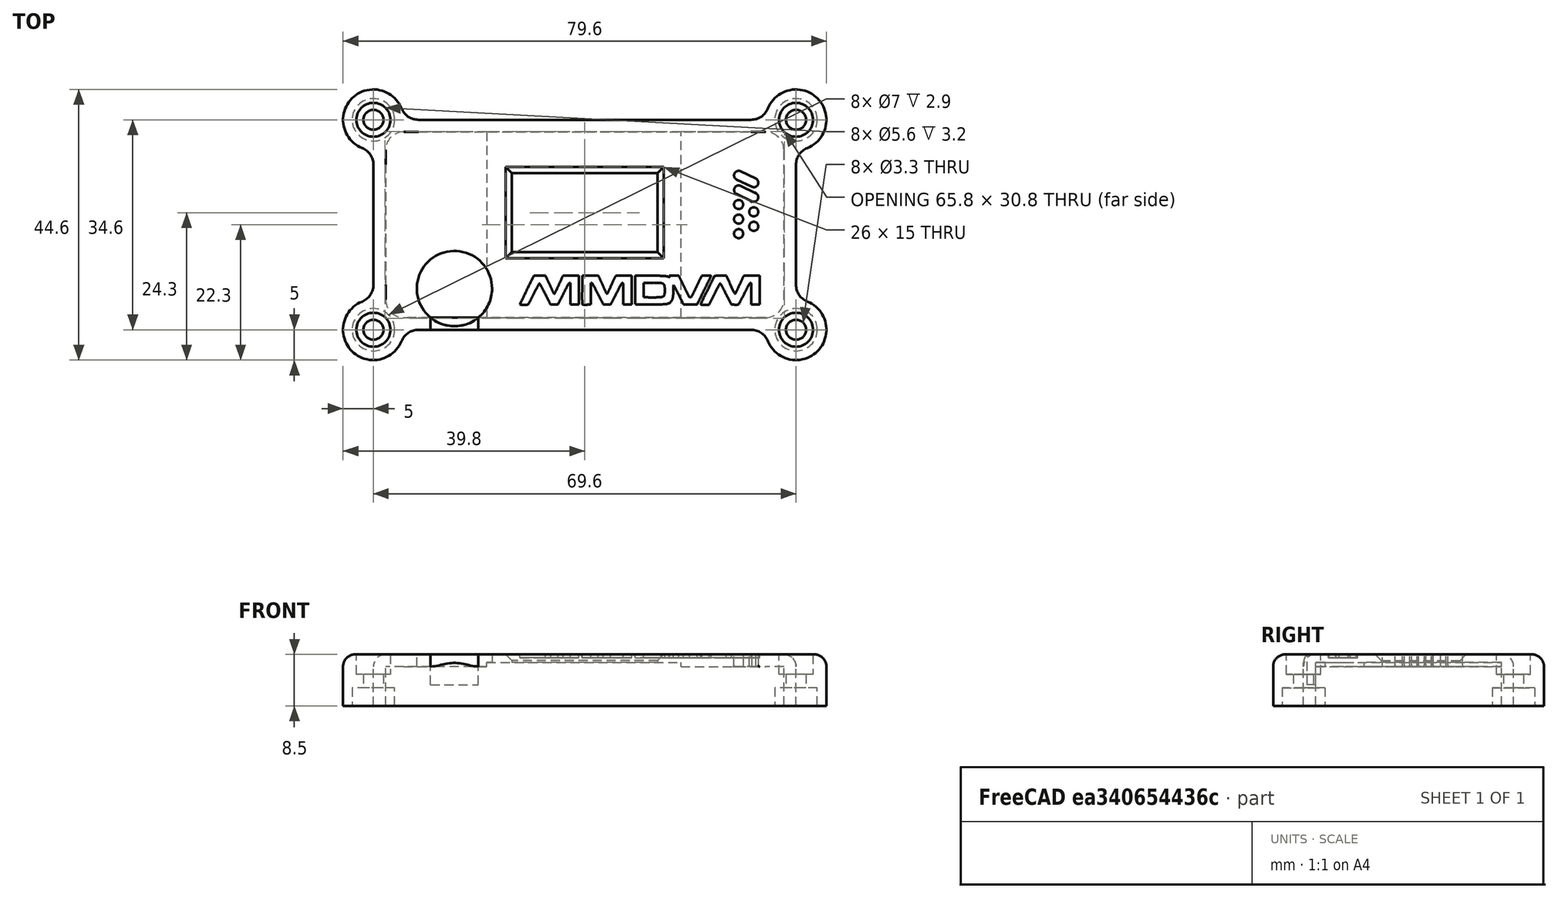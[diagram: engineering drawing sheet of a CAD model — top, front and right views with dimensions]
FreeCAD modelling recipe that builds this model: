
FCSTD DOCUMENT  (FreeCAD 0.18R13934 (Git))
Label: MMDVM_HS_Top-PCB-v1.6-SLIM
License: CreativeCommons Attribution-NonCommercial-ShareAlike
LicenseURL: http://creativecommons.org/licenses/by-nc-sa/4.0/
objects: Sketcher::SketchObject×11, PartDesign::Pocket×6, Part::Feature×5, PartDesign::Fillet×4, Part::Cut×2, Part::FeaturePython×2, PartDesign::Pad×1, PartDesign::Chamfer×1, PartDesign::Hole×1, Part::MultiFuse×1, PartDesign::Body×1, Part::Extrusion×1, Mesh::Feature×1
note: 44 computed .brp shape members not serialized (recipe doc carries the construction recipe); baked Part::Feature solids carry a one-line shape summary decoded from their .brp

FEATURE [Sketcher::SketchObject] Sketch
  MapMode = 5
  Support = -> [XY_Plane]
  sketch-geometry (24):
    g0: LineSegment [constr] StartX=-32.5 StartY=15 StartZ=0 EndX=32.5 EndY=15 EndZ=0
    g1: LineSegment [constr] StartX=32.5 StartY=15 StartZ=0 EndX=32.5 EndY=-15 EndZ=0
    g2: LineSegment [constr] StartX=32.5 StartY=-15 StartZ=0 EndX=-32.5 EndY=-15 EndZ=0
    g3: LineSegment [constr] StartX=-32.5 StartY=-15 StartZ=0 EndX=-32.5 EndY=15 EndZ=0
    g4: LineSegment [constr] StartX=-29 StartY=11.5 StartZ=0 EndX=29 EndY=11.5 EndZ=0
    g5: LineSegment [constr] StartX=29 StartY=11.5 StartZ=0 EndX=29 EndY=-11.5 EndZ=0
    g6: LineSegment [constr] StartX=29 StartY=-11.5 StartZ=0 EndX=-29 EndY=-11.5 EndZ=0
    g7: LineSegment [constr] StartX=-29 StartY=-11.5 StartZ=0 EndX=-29 EndY=11.5 EndZ=0
    g8: Circle CenterX=-29 CenterY=11.5 CenterZ=0 NormalX=0 NormalY=0 NormalZ=1 AngleXU=0 Radius=1.375
    g9: Circle CenterX=29 CenterY=11.5 CenterZ=0 NormalX=0 NormalY=0 NormalZ=1 AngleXU=0 Radius=1.375
    g10: Circle CenterX=29 CenterY=-11.5 CenterZ=0 NormalX=0 NormalY=0 NormalZ=1 AngleXU=0 Radius=1.375
    g11: Circle CenterX=-29 CenterY=-11.5 CenterZ=0 NormalX=0 NormalY=0 NormalZ=1 AngleXU=0 Radius=1.375
    g12: LineSegment [constr] StartX=-29.5 StartY=12 StartZ=0 EndX=29.5 EndY=12 EndZ=0
    g13: LineSegment [constr] StartX=29.5 StartY=12 StartZ=0 EndX=29.5 EndY=-12 EndZ=0
    g14: LineSegment [constr] StartX=29.5 StartY=-12 StartZ=0 EndX=-29.5 EndY=-12 EndZ=0
    g15: LineSegment [constr] StartX=-29.5 StartY=-12 StartZ=0 EndX=-29.5 EndY=12 EndZ=0
    g16: ArcOfCircle CenterX=-29.5 CenterY=12 CenterZ=0 NormalX=0 NormalY=0 NormalZ=1 AngleXU=0 Radius=3 StartAngle=1.5708 EndAngle=3.1416
    g17: ArcOfCircle CenterX=29.5 CenterY=12 CenterZ=0 NormalX=0 NormalY=0 NormalZ=1 AngleXU=0 Radius=3 StartAngle=1.42077e-07 EndAngle=1.5708
    g18: ArcOfCircle CenterX=29.5 CenterY=-12 CenterZ=0 NormalX=0 NormalY=0 NormalZ=1 AngleXU=0 Radius=3 StartAngle=4.71239 EndAngle=6.28319
    g19: ArcOfCircle CenterX=-29.5 CenterY=-12 CenterZ=0 NormalX=0 NormalY=0 NormalZ=1 AngleXU=0 Radius=3 StartAngle=3.14159 EndAngle=4.71239
    g20: LineSegment StartX=-29.5 StartY=15 StartZ=0 EndX=29.5 EndY=15 EndZ=0
    g21: LineSegment StartX=32.5 StartY=12 StartZ=0 EndX=32.5 EndY=-12 EndZ=0
    g22: LineSegment StartX=29.5 StartY=-15 StartZ=0 EndX=-29.5 EndY=-15 EndZ=0
    g23: LineSegment StartX=-32.5 StartY=-12 StartZ=0 EndX=-32.5 EndY=12 EndZ=0
  constraints (68):
    c: Coincident(g0,g1)
    c: Coincident(g1,g2)
    c: Coincident(g2,g3)
    c: Coincident(g3,g0)
    c: Horizontal(g0)
    c: Horizontal(g2)
    c: Vertical(g1)
    c: Vertical(g3)
    c: DistanceX(g0,g0) = 65
    c: DistanceY(g1,g1) = 30
    c: Symmetric(g0,g0,g-2)
    c: Symmetric(g0,g1,g-1)
    c: Coincident(g4,g5)
    c: Coincident(g5,g6)
    c: Coincident(g6,g7)
    c: Coincident(g7,g4)
    c: Horizontal(g4)
    c: Horizontal(g6)
    c: Vertical(g5)
    c: Vertical(g7)
    c: DistanceX(g4,g4) = 58
    c: DistanceY(g5,g5) = 23
    c: Symmetric(g4,g5,g-1)
    c: Symmetric(g4,g4,g-2)
    c: Coincident(g8,g4)
    c: Coincident(g9,g4)
    c: Coincident(g10,g5)
    c: Coincident(g11,g6)
    c: Radius(g11) = 1.375
    c: Radius(g8) = 1.375
    c: Radius(g9) = 1.375
    c: Radius(g10) = 1.375
    c: Coincident(g12,g13)
    c: Coincident(g13,g14)
    c: Coincident(g14,g15)
    c: Coincident(g15,g12)
    c: Horizontal(g12)
    c: Horizontal(g14)
    c: Vertical(g13)
    c: Vertical(g15)
    c: DistanceX(g4,g12) = 0.5
    c: DistanceY(g4,g12) = 0.5
    c: DistanceY(g13,g5) = 0.5
    c: DistanceX(g14,g6) = 0.5
    c: Coincident(g16,g12)
    c: Radius(g16) = 3
    c: Coincident(g17,g12)
    c: Radius(g17) = 3
    c: Coincident(g18,g13)
    c: Radius(g18) = 3
    c: Coincident(g19,g14)
    c: Radius(g19) = 3
    c: PointOnObject(g16,g0)
    c: PointOnObject(g17,g1)
    c: PointOnObject(g18,g2)
    c: PointOnObject(g19,g3)
    c: Coincident(g20,g16)
    c: Horizontal(g20)
    c: Coincident(g20,g17)
    c: Coincident(g21,g17)
    c: Vertical(g21)
    c: Coincident(g18,g21)
    c: Coincident(g22,g18)
    c: Horizontal(g22)
    c: Coincident(g19,g22)
    c: Coincident(g23,g19)
    c: Vertical(g23)
    c: Coincident(g23,g16)
FEATURE [Sketcher::SketchObject] Sketch001
  MapMode = 5
  Support = -> [XY_Plane]
  expr: Constraints[8] = Sketch.Constraints[8]
  expr: Constraints[41] = Sketch.Constraints[41]
  expr: Constraints[9] = Sketch.Constraints[9]
  expr: Constraints[45] = Sketch.Constraints[45]
  expr: Constraints[43] = Sketch.Constraints[43]
  expr: Constraints[42] = Sketch.Constraints[42]
  expr: Constraints[20] = Sketch.Constraints[20]
  expr: Constraints[21] = Sketch.Constraints[21]
  expr: Constraints[28] = Sketch.Constraints[28]
  expr: Constraints[29] = Sketch.Constraints[29]
  expr: Constraints[30] = Sketch.Constraints[30]
  expr: Constraints[40] = Sketch.Constraints[40]
  expr: Constraints[31] = Sketch.Constraints[31]
  expr: Constraints[47] = Sketch.Constraints[47]
  expr: Constraints[49] = Sketch.Constraints[49]
  expr: Constraints[51] = Sketch.Constraints[51]
  sketch-geometry (64):
    g0: LineSegment [constr] StartX=-32.5 StartY=15 StartZ=0 EndX=32.5 EndY=15 EndZ=0
    g1: LineSegment [constr] StartX=32.5 StartY=15 StartZ=0 EndX=32.5 EndY=-15 EndZ=0
    g2: LineSegment [constr] StartX=32.5 StartY=-15 StartZ=0 EndX=-32.5 EndY=-15 EndZ=0
    g3: LineSegment [constr] StartX=-32.5 StartY=-15 StartZ=0 EndX=-32.5 EndY=15 EndZ=0
    g4: LineSegment [constr] StartX=-29 StartY=11.5 StartZ=0 EndX=29 EndY=11.5 EndZ=0
    g5: LineSegment [constr] StartX=29 StartY=11.5 StartZ=0 EndX=29 EndY=-11.5 EndZ=0
    g6: LineSegment [constr] StartX=29 StartY=-11.5 StartZ=0 EndX=-29 EndY=-11.5 EndZ=0
    g7: LineSegment [constr] StartX=-29 StartY=-11.5 StartZ=0 EndX=-29 EndY=11.5 EndZ=0
    g8: Circle [constr] CenterX=-29 CenterY=11.5 CenterZ=0 NormalX=0 NormalY=0 NormalZ=1 AngleXU=0 Radius=1.375
    g9: Circle [constr] CenterX=29 CenterY=11.5 CenterZ=0 NormalX=0 NormalY=0 NormalZ=1 AngleXU=0 Radius=1.375
    g10: Circle [constr] CenterX=29 CenterY=-11.5 CenterZ=0 NormalX=0 NormalY=0 NormalZ=1 AngleXU=0 Radius=1.375
    g11: Circle [constr] CenterX=-29 CenterY=-11.5 CenterZ=0 NormalX=0 NormalY=0 NormalZ=1 AngleXU=0 Radius=1.375
    g12: LineSegment [constr] StartX=-29.5 StartY=12 StartZ=0 EndX=29.5 EndY=12 EndZ=0
    g13: LineSegment [constr] StartX=29.5 StartY=12 StartZ=0 EndX=29.5 EndY=-12 EndZ=0
    g14: LineSegment [constr] StartX=29.5 StartY=-12 StartZ=0 EndX=-29.5 EndY=-12 EndZ=0
    g15: LineSegment [constr] StartX=-29.5 StartY=-12 StartZ=0 EndX=-29.5 EndY=12 EndZ=0
    g16: ArcOfCircle [constr] CenterX=-29.5 CenterY=12 CenterZ=0 NormalX=0 NormalY=0 NormalZ=1 AngleXU=0 Radius=3 StartAngle=1.5708 EndAngle=3.14159
    g17: ArcOfCircle [constr] CenterX=29.5 CenterY=12 CenterZ=0 NormalX=0 NormalY=0 NormalZ=1 AngleXU=0 Radius=3 StartAngle=2.8425e-08 EndAngle=1.5708
    g18: ArcOfCircle [constr] CenterX=29.5 CenterY=-12 CenterZ=0 NormalX=0 NormalY=0 NormalZ=1 AngleXU=0 Radius=3 StartAngle=4.71239 EndAngle=6.28319
    g19: ArcOfCircle [constr] CenterX=-29.5 CenterY=-12 CenterZ=0 NormalX=0 NormalY=0 NormalZ=1 AngleXU=0 Radius=3 StartAngle=3.14159 EndAngle=4.71239
    g20: LineSegment [constr] StartX=-29.5 StartY=15 StartZ=0 EndX=29.5 EndY=15 EndZ=0
    g21: LineSegment [constr] StartX=32.5 StartY=12 StartZ=0 EndX=32.5 EndY=-12 EndZ=0
    g22: LineSegment [constr] StartX=29.5 StartY=-15 StartZ=0 EndX=-29.5 EndY=-15 EndZ=0
    g23: LineSegment [constr] StartX=-32.5 StartY=-12 StartZ=0 EndX=-32.5 EndY=12 EndZ=0
    g24: ArcOfCircle [constr] CenterX=-29.5 CenterY=12 CenterZ=0 NormalX=0 NormalY=0 NormalZ=1 AngleXU=0 Radius=3.3 StartAngle=1.5708 EndAngle=3.14159
    g25: ArcOfCircle [constr] CenterX=29.5 CenterY=12 CenterZ=0 NormalX=0 NormalY=0 NormalZ=1 AngleXU=0 Radius=3.3 StartAngle=-2.2e-10 EndAngle=1.5708
    g26: ArcOfCircle [constr] CenterX=29.5 CenterY=-12 CenterZ=0 NormalX=0 NormalY=0 NormalZ=1 AngleXU=0 Radius=3.3 StartAngle=4.71239 EndAngle=6.28319
    g27: ArcOfCircle [constr] CenterX=-29.5 CenterY=-12 CenterZ=0 NormalX=0 NormalY=0 NormalZ=1 AngleXU=0 Radius=3.3 StartAngle=3.14159 EndAngle=4.71239
    g28: LineSegment [constr] StartX=-32.8 StartY=12 StartZ=0 EndX=-32.8 EndY=-12 EndZ=0
    g29: LineSegment [constr] StartX=-29.5 StartY=15.3 StartZ=0 EndX=29.5 EndY=15.3 EndZ=0
    g30: LineSegment [constr] StartX=32.8 StartY=12 StartZ=0 EndX=32.8 EndY=-12 EndZ=0
    g31: LineSegment [constr] StartX=29.5 StartY=-15.3 StartZ=0 EndX=-29.5 EndY=-15.3 EndZ=0
    g32: LineSegment [constr] StartX=-34.8 StartY=17.3 StartZ=0 EndX=34.8 EndY=17.3 EndZ=0
    g33: LineSegment [constr] StartX=34.8 StartY=17.3 StartZ=0 EndX=34.8 EndY=-17.3 EndZ=0
    g34: LineSegment [constr] StartX=34.8 StartY=-17.3 StartZ=0 EndX=-34.8 EndY=-17.3 EndZ=0
    g35: LineSegment [constr] StartX=-34.8 StartY=-17.3 StartZ=0 EndX=-34.8 EndY=17.3 EndZ=0
    g36: Circle [constr] CenterX=34.8 CenterY=17.3 CenterZ=0 NormalX=0 NormalY=0 NormalZ=1 AngleXU=0 Radius=5
    g37: Circle [constr] CenterX=34.8 CenterY=-17.3 CenterZ=0 NormalX=0 NormalY=0 NormalZ=1 AngleXU=0 Radius=5
    g38: Circle [constr] CenterX=-34.8 CenterY=-17.3 CenterZ=0 NormalX=0 NormalY=0 NormalZ=1 AngleXU=0 Radius=5
    g39: Circle [constr] CenterX=-34.8 CenterY=17.3 CenterZ=0 NormalX=0 NormalY=0 NormalZ=1 AngleXU=0 Radius=5
    g40: Circle [constr] CenterX=27.3838 CenterY=20.3 CenterZ=0 NormalX=0 NormalY=0 NormalZ=1 AngleXU=0 Radius=3
    g41: Circle [constr] CenterX=-27.3838 CenterY=20.3 CenterZ=0 NormalX=0 NormalY=0 NormalZ=1 AngleXU=0 Radius=3
    g42: Circle [constr] CenterX=-37.8 CenterY=9.8838 CenterZ=0 NormalX=0 NormalY=0 NormalZ=1 AngleXU=0 Radius=3
    g43: Circle [constr] CenterX=-37.8 CenterY=-9.8838 CenterZ=0 NormalX=0 NormalY=0 NormalZ=1 AngleXU=0 Radius=3
    g44: Circle [constr] CenterX=-27.3838 CenterY=-20.3 CenterZ=0 NormalX=0 NormalY=0 NormalZ=1 AngleXU=0 Radius=3
    g45: Circle [constr] CenterX=27.3838 CenterY=-20.3 CenterZ=0 NormalX=0 NormalY=0 NormalZ=1 AngleXU=0 Radius=3
    g46: Circle [constr] CenterX=37.8 CenterY=-9.8838 CenterZ=0 NormalX=0 NormalY=0 NormalZ=1 AngleXU=0 Radius=3
    g47: Circle [constr] CenterX=37.8 CenterY=9.8838 CenterZ=0 NormalX=0 NormalY=0 NormalZ=1 AngleXU=0 Radius=3
    g48: ArcOfCircle CenterX=34.8 CenterY=17.3 CenterZ=0 NormalX=0 NormalY=0 NormalZ=1 AngleXU=0 Radius=5 StartAngle=5.09679 EndAngle=9.04038
    g49: ArcOfCircle CenterX=27.3838 CenterY=20.3 CenterZ=0 NormalX=0 NormalY=0 NormalZ=1 AngleXU=0 Radius=3 StartAngle=4.71239 EndAngle=5.89879
    g50: ArcOfCircle CenterX=37.8 CenterY=9.8838 CenterZ=0 NormalX=0 NormalY=0 NormalZ=1 AngleXU=0 Radius=3 StartAngle=1.95519 EndAngle=3.14159
    g51: ArcOfCircle CenterX=37.8 CenterY=-9.8838 CenterZ=0 NormalX=0 NormalY=0 NormalZ=1 AngleXU=0 Radius=3 StartAngle=3.14159 EndAngle=4.32799
    g52: ArcOfCircle CenterX=34.8 CenterY=-17.3 CenterZ=0 NormalX=0 NormalY=0 NormalZ=1 AngleXU=0 Radius=5 StartAngle=3.52599 EndAngle=7.46958
    g53: ArcOfCircle CenterX=27.3838 CenterY=-20.3 CenterZ=0 NormalX=0 NormalY=0 NormalZ=1 AngleXU=0 Radius=3 StartAngle=0.384397 EndAngle=1.5708
    g54: ArcOfCircle CenterX=-27.3838 CenterY=-20.3 CenterZ=0 NormalX=0 NormalY=0 NormalZ=1 AngleXU=0 Radius=3 StartAngle=1.5708 EndAngle=2.7572
    g55: ArcOfCircle CenterX=-34.8 CenterY=-17.3 CenterZ=0 NormalX=0 NormalY=0 NormalZ=1 AngleXU=0 Radius=5 StartAngle=1.95519 EndAngle=5.89879
    g56: ArcOfCircle CenterX=-37.8 CenterY=-9.8838 CenterZ=0 NormalX=0 NormalY=0 NormalZ=1 AngleXU=0 Radius=3 StartAngle=5.09679 EndAngle=6.28319
    g57: ArcOfCircle CenterX=-37.8 CenterY=9.8838 CenterZ=0 NormalX=0 NormalY=0 NormalZ=1 AngleXU=0 Radius=3 StartAngle=6.28319 EndAngle=7.46958
    g58: ArcOfCircle CenterX=-34.8 CenterY=17.3 CenterZ=0 NormalX=0 NormalY=0 NormalZ=1 AngleXU=0 Radius=5 StartAngle=0.384397 EndAngle=4.32799
    g59: ArcOfCircle CenterX=-27.3838 CenterY=20.3 CenterZ=0 NormalX=0 NormalY=0 NormalZ=1 AngleXU=0 Radius=3 StartAngle=3.52599 EndAngle=4.71239
    g60: LineSegment StartX=-27.3838 StartY=17.3 StartZ=0 EndX=27.3838 EndY=17.3 EndZ=0
    g61: LineSegment StartX=34.8 StartY=9.8838 StartZ=0 EndX=34.8 EndY=-9.8838 EndZ=0
    g62: LineSegment StartX=27.3838 StartY=-17.3 StartZ=0 EndX=-27.3838 EndY=-17.3 EndZ=0
    g63: LineSegment StartX=-34.8 StartY=-9.8838 StartZ=0 EndX=-34.8 EndY=9.8838 EndZ=0
  constraints (184):
    c: Coincident(g0,g1)
    c: Coincident(g1,g2)
    c: Coincident(g2,g3)
    c: Coincident(g3,g0)
    c: Horizontal(g0)
    c: Horizontal(g2)
    c: Vertical(g1)
    c: Vertical(g3)
    c: DistanceX(g0,g0) = 65
    c: DistanceY(g1,g1) = 30
    c: Symmetric(g0,g0,g-2)
    c: Symmetric(g0,g1,g-1)
    c: Coincident(g4,g5)
    c: Coincident(g5,g6)
    c: Coincident(g6,g7)
    c: Coincident(g7,g4)
    c: Horizontal(g4)
    c: Horizontal(g6)
    c: Vertical(g5)
    c: Vertical(g7)
    c: DistanceX(g4,g4) = 58
    c: DistanceY(g5,g5) = 23
    c: Symmetric(g4,g5,g-1)
    c: Symmetric(g4,g4,g-2)
    c: Coincident(g8,g4)
    c: Coincident(g9,g4)
    c: Coincident(g10,g5)
    c: Coincident(g11,g6)
    c: Radius(g11) = 1.375
    c: Radius(g8) = 1.375
    c: Radius(g9) = 1.375
    c: Radius(g10) = 1.375
    c: Coincident(g12,g13)
    c: Coincident(g13,g14)
    c: Coincident(g14,g15)
    c: Coincident(g15,g12)
    c: Horizontal(g12)
    c: Horizontal(g14)
    c: Vertical(g13)
    c: Vertical(g15)
    c: DistanceX(g4,g12) = 0.5
    c: DistanceY(g4,g12) = 0.5
    c: DistanceY(g13,g5) = 0.5
    c: DistanceX(g14,g6) = 0.5
    c: Coincident(g16,g12)
    c: Radius(g16) = 3
    c: Coincident(g17,g12)
    c: Radius(g17) = 3
    c: Coincident(g18,g13)
    c: Radius(g18) = 3
    c: Coincident(g19,g14)
    c: Radius(g19) = 3
    c: PointOnObject(g16,g0)
    c: PointOnObject(g17,g1)
    c: PointOnObject(g18,g2)
    c: PointOnObject(g19,g3)
    c: Coincident(g20,g16)
    c: Horizontal(g20)
    c: Coincident(g20,g17)
    c: Coincident(g21,g17)
    c: Vertical(g21)
    c: Coincident(g18,g21)
    c: Coincident(g22,g18)
    c: Horizontal(g22)
    c: Coincident(g19,g22)
    c: Coincident(g23,g19)
    c: Vertical(g23)
    c: Coincident(g23,g16)
    c: Coincident(g24,g12)
    c: Radius(g24) = 3.3
    c: Coincident(g25,g12)
    c: Radius(g25) = 3.3
    c: Coincident(g26,g13)
    c: Radius(g26) = 3.3
    c: Coincident(g27,g14)
    c: Radius(g27) = 3.3
    c: Vertical(g28)
    c: DistanceX(g28,g2) = 0.3
    c: Coincident(g27,g28)
    c: Coincident(g28,g24)
    c: Horizontal(g29)
    c: DistanceY(g0,g29) = 0.3
    c: Coincident(g24,g29)
    c: Coincident(g25,g29)
    c: Vertical(g30)
    c: DistanceX(g0,g30) = 0.3
    c: Coincident(g25,g30)
    c: Coincident(g30,g26)
    c: Horizontal(g31)
    c: DistanceY(g31,g1) = 0.3
    c: Coincident(g31,g26)
    c: Coincident(g31,g27)
    c: Coincident(g32,g33)
    c: Coincident(g33,g34)
    c: Coincident(g34,g35)
    c: Coincident(g35,g32)
    c: Horizontal(g32)
    c: Horizontal(g34)
    c: Vertical(g33)
    c: Vertical(g35)
    c: DistanceY(g25,g32) = 2
    c: DistanceX(g25,g32) = 2
    c: DistanceY(g33,g26) = 2
    c: DistanceX(g34,g27) = 2
    c: Coincident(g36,g32)
    c: Coincident(g37,g33)
    c: Coincident(g38,g34)
    c: Coincident(g39,g32)
    c: Radius(g39) = 5
    c: Radius(g38) = 5
    c: Radius(g37) = 5
    c: Radius(g36) = 5
    c: Radius(g40) = 3
    c: Tangent(g40,g36)
    c: Tangent(g40,g32)
    c: Tangent(g47,g36)
    c: Radius(g47) = 3
    c: Tangent(g47,g33)
    c: Radius(g46) = 3
    c: Tangent(g46,g37)
    c: Tangent(g46,g33)
    c: Radius(g45) = 3
    c: Tangent(g45,g37)
    c: Tangent(g45,g34)
    c: Radius(g44) = 3
    c: Tangent(g44,g34)
    c: Tangent(g44,g38)
    c: Radius(g43) = 3
    c: Tangent(g43,g38)
    c: Tangent(g43,g35)
    c: Radius(g42) = 3
    c: Tangent(g42,g35)
    c: Tangent(g42,g39)
    c: Radius(g41) = 3
    c: Tangent(g41,g32)
    c: Tangent(g41,g39)
    c: Coincident(g48,g32)
    c: PointOnObject(g48,g36)
    c: Coincident(g49,g40)
    c: PointOnObject(g49,g40)
    c: Coincident(g50,g47)
    c: PointOnObject(g50,g47)
    c: Coincident(g51,g46)
    c: PointOnObject(g51,g46)
    c: Coincident(g52,g33)
    c: PointOnObject(g52,g37)
    c: Coincident(g53,g45)
    c: PointOnObject(g53,g45)
    c: Coincident(g54,g44)
    c: PointOnObject(g54,g44)
    c: Coincident(g55,g34)
    c: PointOnObject(g55,g38)
    c: Coincident(g56,g43)
    c: PointOnObject(g56,g43)
    c: Coincident(g57,g42)
    c: PointOnObject(g57,g42)
    c: Coincident(g58,g32)
    c: PointOnObject(g58,g39)
    c: Coincident(g59,g41)
    c: PointOnObject(g59,g41)
    c: Coincident(g49,g48)
    c: Coincident(g48,g50)
    c: Coincident(g51,g52)
    c: Coincident(g52,g53)
    c: Coincident(g54,g55)
    c: Coincident(g55,g56)
    c: Coincident(g57,g58)
    c: Coincident(g58,g59)
    c: PointOnObject(g60,g32)
    c: Horizontal(g60)
    c: PointOnObject(g61,g33)
    c: Vertical(g61)
    c: PointOnObject(g62,g34)
    c: Horizontal(g62)
    c: PointOnObject(g63,g35)
    c: Vertical(g63)
    c: Coincident(g59,g60)
    c: Coincident(g60,g49)
    c: Coincident(g50,g61)
    c: Coincident(g61,g51)
    c: Coincident(g53,g62)
    c: Coincident(g54,g62)
    c: Coincident(g56,g63)
    c: Coincident(g57,g63)
FEATURE [PartDesign::Pad] Pad
  Length = 8.5
  Length2 = 100
  Profile = -> Sketch001
  Type = 0
FEATURE [Sketcher::SketchObject] Sketch002
  ExternalGeometry = -> [Pad]
  MapMode = 5
  Placement = pos=(0,0,0) rot=(1,0,0;3.14159rad)
  Support = -> [Pad]
  sketch-geometry (4):
    g0: Circle CenterX=34.8 CenterY=17.3 CenterZ=0 NormalX=0 NormalY=0 NormalZ=1 AngleXU=0 Radius=3.5
    g1: Circle CenterX=34.8 CenterY=-17.3 CenterZ=0 NormalX=0 NormalY=0 NormalZ=1 AngleXU=0 Radius=3.5
    g2: Circle CenterX=-34.8 CenterY=-17.3 CenterZ=0 NormalX=0 NormalY=0 NormalZ=1 AngleXU=0 Radius=3.5
    g3: Circle CenterX=-34.8 CenterY=17.3 CenterZ=0 NormalX=0 NormalY=0 NormalZ=1 AngleXU=0 Radius=3.5
  constraints (8):
    c: Coincident(g0,g-3)
    c: Radius(g0) = 3.5
    c: Coincident(g1,g-6)
    c: Radius(g1) = 3.5
    c: Coincident(g2,g-5)
    c: Radius(g2) = 3.5
    c: Coincident(g3,g-4)
    c: Radius(g3) = 3.5
FEATURE [PartDesign::Pocket] Pocket
  BaseFeature = -> Pad
  Length = 3
  Length2 = 1
  Profile = -> Sketch002
  Type = 0
FEATURE [Sketcher::SketchObject] Sketch003
  MapMode = 5
  Placement = pos=(0,0,0) rot=(1,0,0;3.14159rad)
  Support = -> [Pocket]
  expr: Constraints[8] = Sketch.Constraints[8]
  expr: Constraints[39] = Sketch.Constraints[40]
  expr: Constraints[30] = Sketch.Constraints[31]
  expr: Constraints[27] = Sketch.Constraints[28]
  expr: Constraints[29] = Sketch.Constraints[30]
  expr: Constraints[28] = Sketch.Constraints[29]
  expr: Constraints[20] = -Sketch.Constraints[21]
  expr: Constraints[19] = Sketch.Constraints[20]
  expr: Constraints[42] = Sketch.Constraints[43]
  expr: Constraints[41] = -Sketch.Constraints[42]
  expr: Constraints[9] = -Sketch.Constraints[9]
  expr: Constraints[40] = -Sketch.Constraints[41]
  sketch-geometry (32):
    g0: LineSegment [constr] StartX=-32.5 StartY=-15 StartZ=0 EndX=32.5 EndY=-15 EndZ=0
    g1: LineSegment [constr] StartX=32.5 StartY=-15 StartZ=0 EndX=32.5 EndY=15 EndZ=0
    g2: LineSegment [constr] StartX=32.5 StartY=15 StartZ=0 EndX=-32.5 EndY=15 EndZ=0
    g3: LineSegment [constr] StartX=-32.5 StartY=15 StartZ=0 EndX=-32.5 EndY=-15 EndZ=0
    g4: LineSegment [constr] StartX=-29 StartY=-11.5 StartZ=0 EndX=29 EndY=-11.5 EndZ=0
    g5: LineSegment [constr] StartX=29 StartY=-11.5 StartZ=0 EndX=29 EndY=11.5 EndZ=0
    g6: LineSegment [constr] StartX=29 StartY=11.5 StartZ=0 EndX=-29 EndY=11.5 EndZ=0
    g7: LineSegment [constr] StartX=-29 StartY=11.5 StartZ=0 EndX=-29 EndY=-11.5 EndZ=0
    g8: Circle [constr] CenterX=-29 CenterY=-11.5 CenterZ=0 NormalX=0 NormalY=0 NormalZ=1 AngleXU=0 Radius=1.375
    g9: Circle [constr] CenterX=29 CenterY=-11.5 CenterZ=0 NormalX=0 NormalY=0 NormalZ=1 AngleXU=0 Radius=1.375
    g10: Circle [constr] CenterX=29 CenterY=11.5 CenterZ=0 NormalX=0 NormalY=0 NormalZ=1 AngleXU=0 Radius=1.375
    g11: Circle [constr] CenterX=-29 CenterY=11.5 CenterZ=0 NormalX=0 NormalY=0 NormalZ=1 AngleXU=0 Radius=1.375
    g12: LineSegment [constr] StartX=-29.5 StartY=-12 StartZ=0 EndX=29.5 EndY=-12 EndZ=0
    g13: LineSegment [constr] StartX=29.5 StartY=-12 StartZ=0 EndX=29.5 EndY=12 EndZ=0
    g14: LineSegment [constr] StartX=29.5 StartY=12 StartZ=0 EndX=-29.5 EndY=12 EndZ=0
    g15: LineSegment [constr] StartX=-29.5 StartY=12 StartZ=0 EndX=-29.5 EndY=-12 EndZ=0
    g16: LineSegment [constr] StartX=-29.5121 StartY=-15 StartZ=0 EndX=29.5 EndY=-15 EndZ=0
    g17: LineSegment [constr] StartX=32.5 StartY=-12 StartZ=0 EndX=32.5 EndY=12 EndZ=0
    g18: LineSegment [constr] StartX=29.5 StartY=15 StartZ=0 EndX=-29.5121 EndY=15 EndZ=0
    g19: LineSegment [constr] StartX=-32.5 StartY=12 StartZ=0 EndX=-32.5 EndY=-12 EndZ=0
    g20: ArcOfCircle [constr] CenterX=-29.5 CenterY=12 CenterZ=0 NormalX=0 NormalY=0 NormalZ=1 AngleXU=0 Radius=3.00002 StartAngle=1.57483 EndAngle=3.1416
    g21: ArcOfCircle [constr] CenterX=29.5 CenterY=12 CenterZ=0 NormalX=0 NormalY=0 NormalZ=1 AngleXU=0 Radius=3 StartAngle=6.28318 EndAngle=7.85399
    g22: ArcOfCircle [constr] CenterX=29.5 CenterY=-12 CenterZ=0 NormalX=0 NormalY=0 NormalZ=1 AngleXU=0 Radius=3 StartAngle=4.71238 EndAngle=6.28319
    g23: ArcOfCircle [constr] CenterX=-29.5 CenterY=-12 CenterZ=0 NormalX=0 NormalY=0 NormalZ=1 AngleXU=0 Radius=3.00002 StartAngle=3.14159 EndAngle=4.70836
    g24: LineSegment StartX=-29.8 StartY=15.3 StartZ=0 EndX=29.8 EndY=15.3 EndZ=0
    g25: LineSegment StartX=32.8 StartY=12.3 StartZ=0 EndX=32.8 EndY=-12.3 EndZ=0
    g26: LineSegment StartX=29.8 StartY=-15.3 StartZ=0 EndX=-29.8 EndY=-15.3 EndZ=0
    g27: LineSegment StartX=-32.8 StartY=-12.3 StartZ=0 EndX=-32.8 EndY=12.3 EndZ=0
    g28: ArcOfCircle CenterX=29.8 CenterY=12.3 CenterZ=0 NormalX=0 NormalY=0 NormalZ=1 AngleXU=0 Radius=3 StartAngle=0 EndAngle=1.5708
    g29: ArcOfCircle CenterX=29.8 CenterY=-12.3 CenterZ=0 NormalX=0 NormalY=0 NormalZ=1 AngleXU=0 Radius=3 StartAngle=4.71239 EndAngle=6.28319
    g30: ArcOfCircle CenterX=-29.8 CenterY=-12.3 CenterZ=0 NormalX=0 NormalY=0 NormalZ=1 AngleXU=0 Radius=3 StartAngle=3.14159 EndAngle=4.71239
    g31: ArcOfCircle CenterX=-29.8 CenterY=12.3 CenterZ=0 NormalX=0 NormalY=0 NormalZ=1 AngleXU=0 Radius=3 StartAngle=1.5708 EndAngle=3.14159
  constraints (83):
    c: Coincident(g0,g1)
    c: Coincident(g1,g2)
    c: Coincident(g2,g3)
    c: Coincident(g3,g0)
    c: Horizontal(g0)
    c: Horizontal(g2)
    c: Vertical(g1)
    c: Vertical(g3)
    c: DistanceX(g0,g0) = 65
    c: DistanceY(g1,g1) = -30
    c: Symmetric(g0,g0,g-2)
    c: Symmetric(g0,g1,g-1)
    c: Coincident(g4,g5)
    c: Coincident(g5,g6)
    c: Coincident(g6,g7)
    c: Horizontal(g4)
    c: Horizontal(g6)
    c: Vertical(g5)
    c: Vertical(g7)
    c: DistanceX(g4,g4) = 58
    c: DistanceY(g5,g5) = -23
    c: Symmetric(g4,g5,g-1)
    c: Symmetric(g4,g4,g-2)
    c: Coincident(g8,g4)
    c: Coincident(g9,g4)
    c: Coincident(g10,g5)
    c: Coincident(g11,g6)
    c: Radius(g11) = 1.375
    c: Radius(g8) = 1.375
    c: Radius(g9) = 1.375
    c: Radius(g10) = 1.375
    c: Coincident(g12,g13)
    c: Coincident(g13,g14)
    c: Coincident(g14,g15)
    c: Coincident(g15,g12)
    c: Horizontal(g12)
    c: Horizontal(g14)
    c: Vertical(g13)
    c: Vertical(g15)
    c: DistanceX(g4,g12) = 0.5
    c: DistanceY(g4,g12) = -0.5
    c: DistanceY(g13,g5) = -0.5
    c: DistanceX(g14,g6) = 0.5
    c: PointOnObject(g16,g0)
    c: PointOnObject(g17,g1)
    c: PointOnObject(g18,g2)
    c: PointOnObject(g19,g3)
    c: Horizontal(g16)
    c: Vertical(g17)
    c: Horizontal(g18)
    c: Vertical(g19)
    c: Coincident(g20,g14)
    c: Coincident(g20,g18)
    c: Coincident(g20,g19)
    c: Coincident(g21,g13)
    c: Coincident(g21,g17)
    c: Coincident(g21,g18)
    c: Coincident(g22,g12)
    c: Coincident(g22,g16)
    c: Coincident(g22,g17)
    c: Coincident(g23,g12)
    c: Coincident(g23,g19)
    c: Coincident(g23,g16)
    c: Horizontal(g24)
    c: Horizontal(g26)
    c: Vertical(g25)
    c: Vertical(g27)
    c: Tangent(g24,g28) = 1.5708
    c: Tangent(g25,g28) = 1.5708
    c: Tangent(g25,g29) = 1.5708
    c: Tangent(g26,g29) = 1.5708
    c: Tangent(g26,g30) = 1.5708
    c: Tangent(g27,g30) = 1.5708
    c: Tangent(g27,g31) = 1.5708
    c: Tangent(g24,g31) = 1.5708
    c: Radius(g31) = 3
    c: Radius(g28) = 3
    c: Radius(g29) = 3
    c: Radius(g30) = 3
    c: DistanceY(g1,g24) = 0.3
    c: DistanceX(g17,g25) = 0.3
    c: DistanceY(g26,g16) = 0.3
    c: DistanceX(g27,g19) = 0.3
FEATURE [PartDesign::Pocket] Pocket001
  BaseFeature = -> Pocket
  Length = 6.5
  Length2 = 100
  Profile = -> Sketch003
  Type = 0
FEATURE [Sketcher::SketchObject] Sketch004
  ExternalGeometry = -> [Pocket001]
  MapMode = 5
  Placement = pos=(0,0,8.5) rot=(0,0,1;0rad)
  Support = -> [Pocket001]
  sketch-geometry (32):
    g0: LineSegment StartX=-27.3838 StartY=17.3 StartZ=0 EndX=-31.8 EndY=17.3 EndZ=0
    g1: LineSegment StartX=-34.8 StartY=9.8838 StartZ=0 EndX=-34.8 EndY=14.3 EndZ=0
    g2: Circle [constr] CenterX=-31.8 CenterY=14.3 CenterZ=0 NormalX=0 NormalY=0 NormalZ=1 AngleXU=0 Radius=3
    g3: ArcOfCircle CenterX=-31.8 CenterY=14.3 CenterZ=0 NormalX=0 NormalY=0 NormalZ=1 AngleXU=0 Radius=3 StartAngle=1.5708 EndAngle=3.14159
    g4: LineSegment StartX=-41.7809 StartY=24.2149 StartZ=0 EndX=-27.3838 EndY=24.2149 EndZ=0
    g5: LineSegment StartX=-41.7809 StartY=9.8838 StartZ=0 EndX=-41.7809 EndY=24.2149 EndZ=0
    g6: LineSegment StartX=-27.3838 StartY=24.2149 StartZ=0 EndX=-27.3838 EndY=17.3 EndZ=0
    g7: LineSegment StartX=-41.7809 StartY=9.8838 StartZ=0 EndX=-34.8 EndY=9.8838 EndZ=0
    g8: LineSegment StartX=27.3838 StartY=17.3 StartZ=0 EndX=31.8 EndY=17.3 EndZ=0
    g9: LineSegment StartX=34.8 StartY=9.8838 StartZ=0 EndX=34.8 EndY=14.3 EndZ=0
    g10: Circle [constr] CenterX=31.8 CenterY=14.3 CenterZ=0 NormalX=0 NormalY=0 NormalZ=1 AngleXU=0 Radius=3
    g11: ArcOfCircle CenterX=31.8 CenterY=14.3 CenterZ=0 NormalX=0 NormalY=0 NormalZ=1 AngleXU=0 Radius=3 StartAngle=4.4834e-08 EndAngle=1.5708
    g12: LineSegment StartX=41.7622 StartY=24.6512 StartZ=0 EndX=27.3838 EndY=24.6512 EndZ=0
    g13: LineSegment StartX=41.7622 StartY=9.8838 StartZ=0 EndX=41.7622 EndY=24.6512 EndZ=0
    g14: LineSegment StartX=27.3838 StartY=24.6512 StartZ=0 EndX=27.3838 EndY=17.3 EndZ=0
    g15: LineSegment StartX=41.7622 StartY=9.8838 StartZ=0 EndX=34.8 EndY=9.8838 EndZ=0
    g16: LineSegment StartX=-34.8 StartY=-9.8838 StartZ=0 EndX=-34.8 EndY=-14.3 EndZ=0
    g17: LineSegment StartX=-27.3838 StartY=-17.3 StartZ=0 EndX=-31.8 EndY=-17.3 EndZ=0
    g18: Circle [constr] CenterX=-31.8 CenterY=-14.3 CenterZ=0 NormalX=0 NormalY=0 NormalZ=1 AngleXU=0 Radius=3
    g19: ArcOfCircle CenterX=-31.8 CenterY=-14.3 CenterZ=0 NormalX=0 NormalY=0 NormalZ=1 AngleXU=0 Radius=3 StartAngle=3.14159 EndAngle=4.71239
    g20: LineSegment StartX=-27.3838 StartY=-24.2044 StartZ=0 EndX=-41.4724 EndY=-24.2044 EndZ=0
    g21: LineSegment StartX=-41.4724 StartY=-24.2044 StartZ=0 EndX=-41.4724 EndY=-9.8838 EndZ=0
    g22: LineSegment StartX=-41.4724 StartY=-9.8838 StartZ=0 EndX=-34.8 EndY=-9.8838 EndZ=0
    g23: LineSegment StartX=-27.3838 StartY=-24.2044 StartZ=0 EndX=-27.3838 EndY=-17.3 EndZ=0
    g24: LineSegment StartX=34.8 StartY=-9.8838 StartZ=0 EndX=34.8 EndY=-14.3 EndZ=0
    g25: LineSegment StartX=27.3838 StartY=-17.3 StartZ=0 EndX=31.8 EndY=-17.3 EndZ=0
    g26: Circle [constr] CenterX=31.8 CenterY=-14.3 CenterZ=0 NormalX=0 NormalY=0 NormalZ=1 AngleXU=0 Radius=3
    g27: ArcOfCircle CenterX=31.8 CenterY=-14.3 CenterZ=0 NormalX=0 NormalY=0 NormalZ=1 AngleXU=0 Radius=3 StartAngle=4.71239 EndAngle=6.28319
    g28: LineSegment StartX=41.5436 StartY=-23.6904 StartZ=0 EndX=27.3838 EndY=-23.6904 EndZ=0
    g29: LineSegment StartX=41.5436 StartY=-9.8838 StartZ=0 EndX=41.5436 EndY=-23.6904 EndZ=0
    g30: LineSegment StartX=41.5436 StartY=-9.8838 StartZ=0 EndX=34.8 EndY=-9.8838 EndZ=0
    g31: LineSegment StartX=27.3838 StartY=-23.6904 StartZ=0 EndX=27.3838 EndY=-17.3 EndZ=0
  constraints (88):
    c: PointOnObject(g0,g-3)
    c: Horizontal(g0)
    c: PointOnObject(g1,g-6)
    c: Vertical(g1)
    c: Radius(g2) = 3
    c: Tangent(g2,g0)
    c: Tangent(g2,g1)
    c: Coincident(g3,g2)
    c: PointOnObject(g3,g2)
    c: Coincident(g3,g1)
    c: Coincident(g3,g0)
    c: Coincident(g5,g4)
    c: Horizontal(g4)
    c: Vertical(g5)
    c: Coincident(g6,g4)
    c: Vertical(g6)
    c: Coincident(g7,g5)
    c: Horizontal(g7)
    c: Coincident(g7,g1)
    c: Coincident(g6,g0)
    c: PointOnObject(g8,g-3)
    c: Horizontal(g8)
    c: PointOnObject(g9,g-4)
    c: Vertical(g9)
    c: Radius(g10) = 3
    c: Tangent(g10,g8)
    c: Tangent(g10,g9)
    c: Coincident(g11,g10)
    c: PointOnObject(g11,g10)
    c: Coincident(g11,g8)
    c: Coincident(g11,g9)
    c: Coincident(g13,g12)
    c: Horizontal(g12)
    c: Vertical(g13)
    c: Coincident(g14,g12)
    c: Vertical(g14)
    c: Coincident(g15,g13)
    c: Horizontal(g15)
    c: Coincident(g15,g9)
    c: Coincident(g14,g8)
    c: PointOnObject(g16,g-6)
    c: Vertical(g16)
    c: PointOnObject(g17,g-5)
    c: Horizontal(g17)
    c: Radius(g18) = 3
    c: Tangent(g18,g16)
    c: Tangent(g18,g17)
    c: Coincident(g19,g18)
    c: PointOnObject(g19,g18)
    c: Coincident(g19,g17)
    c: Coincident(g19,g16)
    c: Coincident(g20,g21)
    c: Horizontal(g20)
    c: Vertical(g21)
    c: Coincident(g22,g21)
    c: Horizontal(g22)
    c: Coincident(g23,g20)
    c: Vertical(g23)
    c: Coincident(g23,g17)
    c: Coincident(g22,g16)
    c: PointOnObject(g24,g-4)
    c: Vertical(g24)
    c: PointOnObject(g25,g-5)
    c: Horizontal(g25)
    c: Radius(g26) = 3
    c: Tangent(g26,g24)
    c: Tangent(g26,g25)
    c: Coincident(g27,g26)
    c: PointOnObject(g27,g26)
    c: Coincident(g27,g24)
    c: Coincident(g27,g25)
    c: Coincident(g29,g28)
    c: Horizontal(g28)
    c: Vertical(g29)
    c: Coincident(g30,g29)
    c: Horizontal(g30)
    c: Coincident(g31,g28)
    c: Vertical(g31)
    c: Coincident(g31,g25)
    c: Coincident(g30,g24)
    c: Coincident(g0,g-3)
    c: Coincident(g1,g-6)
    c: Coincident(g-6,g16)
    c: Coincident(g17,g-5)
    c: Coincident(g-5,g25)
    c: Coincident(g-4,g24)
    c: Coincident(g9,g-4)
    c: Coincident(g8,g-3)
FEATURE [Sketcher::SketchObject] Sketch005
  ExternalGeometry = -> [Pocket001,Sketch]
  MapMode = 5
  Placement = pos=(0,0,8.5) rot=(0,0,1;0rad)
  Support = -> [Pocket001]
  sketch-geometry (10):
    g0: LineSegment [constr] StartX=-21.4583 StartY=31.2328 StartZ=0 EndX=-21.4583 EndY=-27.0552 EndZ=0
    g1: LineSegment [constr] StartX=-45.4064 StartY=-10.5129 StartZ=0 EndX=40.4454 EndY=-10.5129 EndZ=0
    g2: Circle [constr] CenterX=-21.4583 CenterY=-10.5129 CenterZ=0 NormalX=0 NormalY=0 NormalZ=1 AngleXU=0 Radius=6.2
    g3: LineSegment StartX=-12 StartY=8.5 StartZ=0 EndX=12 EndY=8.5 EndZ=0
    g4: LineSegment StartX=12 StartY=8.5 StartZ=0 EndX=12 EndY=-4.5 EndZ=0
    g5: LineSegment StartX=12 StartY=-4.5 StartZ=0 EndX=-12 EndY=-4.5 EndZ=0
    g6: LineSegment StartX=-12 StartY=-4.5 StartZ=0 EndX=-12 EndY=8.5 EndZ=0
    g7: LineSegment [constr] StartX=-29 StartY=24.9491 StartZ=0 EndX=-29 EndY=-20.674 EndZ=0
    g8: LineSegment [constr] StartX=-44.8443 StartY=11.5 StartZ=0 EndX=14.9752 EndY=11.5 EndZ=0
    g9: Circle CenterX=-21.4583 CenterY=-10.5129 CenterZ=0 NormalX=0 NormalY=0 NormalZ=1 AngleXU=0 Radius=6.2
  constraints (26):
    c: Coincident(g5,g6)
    c: Coincident(g3,g6)
    c: Coincident(g4,g5)
    c: Coincident(g3,g4)
    c: DistanceX(g3,g3) = 24
    c: DistanceY(g4,g4) = 13
    c: Vertical(g7)
    c: Horizontal(g8)
    c: PointOnObject(g-4,g8)
    c: PointOnObject(g-4,g7)
    c: PointOnObject(g2,g0)
    c: PointOnObject(g2,g1)
    c: DistanceX(g7,g0) = 7.54172
    c: DistanceX(g7,g3) = 17
    c: DistanceY(g3,g-4) = 3
    c: DistanceY(g1,g8) = 22.0129
    c: Vertical(g0)
    c: Horizontal(g1)
    c: Radius(g2) = 6.2
    c: Coincident(g9,g2)
    c: Radius(g9) = 6.2
    c: DistanceY(g-5,g-4) = 23
    c: Vertical(g4)
    c: Vertical(g6)
    c: Horizontal(g3)
    c: Horizontal(g5)
FEATURE [PartDesign::Pocket] Pocket002
  BaseFeature = -> Pocket001
  Length = 5
  Length2 = 100
  Profile = -> Sketch005
  Type = 0
FEATURE [Sketcher::SketchObject] Sketch006
  AttachmentOffset = pos=(7.7,0,0) rot=(0,0,1;0rad)
  ExternalGeometry = -> [Pocket002]
  MapMode = 5
  Placement = pos=(7.7,0,6.5) rot=(1,0,0;3.14159rad)
  Support = -> [Pocket002]
  sketch-geometry (4):
    g0: LineSegment StartX=-23.85 StartY=15.3 StartZ=0 EndX=8.15 EndY=15.3 EndZ=0
    g1: LineSegment StartX=8.15 StartY=15.3 StartZ=0 EndX=8.15 EndY=-15.3 EndZ=0
    g2: LineSegment StartX=8.15 StartY=-15.3 StartZ=0 EndX=-23.85 EndY=-15.3 EndZ=0
    g3: LineSegment StartX=-23.85 StartY=-15.3 StartZ=0 EndX=-23.85 EndY=15.3 EndZ=0
FEATURE [PartDesign::Pocket] Pocket003
  BaseFeature = -> Pocket002
  Length = 0.7
  Length2 = 100
  Profile = -> Sketch006
  Type = 0
FEATURE [PartDesign::Fillet] Fillet
  Base = -> Pocket003 [Edge38]
  BaseFeature = -> Pocket003
  Radius = 2
FEATURE [PartDesign::Chamfer] Chamfer
  Base = -> Fillet [Edge60,Edge61,Edge62,Edge63]
  BaseFeature = -> Fillet
  Size = 1
FEATURE [Sketcher::SketchObject] Sketch007
  MapMode = 5
  Placement = pos=(0,0,15.5) rot=(0,0,1;0rad)
  sketch-geometry (4):
    g0: Circle CenterX=34.8 CenterY=17.3 CenterZ=0 NormalX=0 NormalY=0 NormalZ=1 AngleXU=0 Radius=2.63102
    g1: Circle CenterX=-34.8 CenterY=17.3 CenterZ=0 NormalX=0 NormalY=0 NormalZ=1 AngleXU=0 Radius=2.66333
    g2: Circle CenterX=-34.8 CenterY=-17.3 CenterZ=0 NormalX=0 NormalY=0 NormalZ=1 AngleXU=0 Radius=2.82775
    g3: Circle CenterX=34.8 CenterY=-17.3 CenterZ=0 NormalX=0 NormalY=0 NormalZ=1 AngleXU=0 Radius=2.89107
FEATURE [PartDesign::Hole] Hole
  BaseFeature = -> Chamfer
  Depth = 20
  DepthType = 1
  Diameter = 3.3
  DrillPoint = 1
  DrillPointAngle = 118
  HoleCutCountersinkAngle = 90
  HoleCutDepth = 0
  HoleCutDiameter = 3
  HoleCutType = 0
  ModelActualThread = false
  Profile = -> Sketch007
  Tapered = false
  TaperedAngle = 90
  ThreadAngle = 60
  ThreadClass = 0
  ThreadCutOffInner = 0.0433013
  ThreadCutOffOuter = 0.0866025
  ThreadDirection = 0
  ThreadFit = 0
  ThreadPitch = 0.4
  ThreadSize = 3
  ThreadType = 1
  Threaded = false
FEATURE [Sketcher::SketchObject] Sketch008
  ExternalGeometry = -> [Hole]
  MapMode = 5
  Placement = pos=(0,0,8.5) rot=(0,0,1;0rad)
  Support = -> [Hole]
  sketch-geometry (4):
    g0: Circle CenterX=34.8 CenterY=17.3 CenterZ=0 NormalX=0 NormalY=0 NormalZ=1 AngleXU=0 Radius=2.8
    g1: Circle CenterX=34.8 CenterY=-17.3 CenterZ=0 NormalX=0 NormalY=0 NormalZ=1 AngleXU=0 Radius=2.8
    g2: Circle CenterX=-34.8 CenterY=-17.3 CenterZ=0 NormalX=0 NormalY=0 NormalZ=1 AngleXU=0 Radius=2.8
    g3: Circle CenterX=-34.8 CenterY=17.3 CenterZ=0 NormalX=0 NormalY=0 NormalZ=1 AngleXU=0 Radius=2.8
  constraints (7):
    c: Coincident(g0,g-5)
    c: Coincident(g1,g-8)
    c: Coincident(g3,g-6)
    c: Radius(g3) = 2.8
    c: Radius(g0) = 2.8
    c: Radius(g2) = 2.8
    c: Radius(g1) = 2.8
FEATURE [PartDesign::Pocket] Pocket004
  BaseFeature = -> Hole
  Length = 3.3
  Length2 = 100
  Profile = -> Sketch008
  Type = 0
FEATURE [Sketcher::SketchObject] Sketch009
  MapMode = 5
  Placement = pos=(0,0,8.5) rot=(0,0,1;0rad)
  Support = -> [Pocket004]
  expr: Constraints[38] = Sketch.Constraints[42]
  expr: Constraints[16] = Sketch.Constraints[20]
  expr: Constraints[17] = Sketch.Constraints[21]
  expr: Constraints[25] = Sketch.Constraints[29]
  expr: Constraints[27] = Sketch.Constraints[31]
  expr: Constraints[26] = Sketch.Constraints[30]
  expr: Constraints[6] = Sketch.Constraints[8]
  expr: Constraints[36] = Sketch.Constraints[40]
  expr: Constraints[7] = Sketch.Constraints[9]
  expr: Constraints[24] = Sketch.Constraints[28]
  expr: Constraints[47] = Sketch.Constraints[51]
  expr: Constraints[39] = Sketch.Constraints[43]
  expr: Constraints[37] = Sketch.Constraints[41]
  expr: Constraints[43] = Sketch.Constraints[47]
  expr: Constraints[45] = Sketch.Constraints[49]
  expr: Constraints[41] = Sketch.Constraints[45]
  sketch-geometry (62):
    g0: LineSegment [constr] StartX=-32.5 StartY=15 StartZ=0 EndX=32.5 EndY=15 EndZ=0
    g1: LineSegment [constr] StartX=32.5 StartY=15 StartZ=0 EndX=32.5 EndY=-15 EndZ=0
    g2: LineSegment [constr] StartX=32.5 StartY=-15 StartZ=0 EndX=-32.5 EndY=-15 EndZ=0
    g3: LineSegment [constr] StartX=-32.5 StartY=-15 StartZ=0 EndX=-32.5 EndY=15 EndZ=0
    g4: LineSegment [constr] StartX=-29 StartY=11.5 StartZ=0 EndX=29 EndY=11.5 EndZ=0
    g5: LineSegment [constr] StartX=29 StartY=11.5 StartZ=0 EndX=29 EndY=-11.5 EndZ=0
    g6: LineSegment [constr] StartX=29 StartY=-11.5 StartZ=0 EndX=-29 EndY=-11.5 EndZ=0
    g7: LineSegment [constr] StartX=-29 StartY=-11.5 StartZ=0 EndX=-29 EndY=11.5 EndZ=0
    g8: Circle [constr] CenterX=-29 CenterY=11.5 CenterZ=0 NormalX=0 NormalY=0 NormalZ=1 AngleXU=0 Radius=1.375
    g9: Circle [constr] CenterX=29 CenterY=11.5 CenterZ=0 NormalX=0 NormalY=0 NormalZ=1 AngleXU=0 Radius=1.375
    g10: Circle [constr] CenterX=29 CenterY=-11.5 CenterZ=0 NormalX=0 NormalY=0 NormalZ=1 AngleXU=0 Radius=1.375
    g11: Circle [constr] CenterX=-29 CenterY=-11.5 CenterZ=0 NormalX=0 NormalY=0 NormalZ=1 AngleXU=0 Radius=1.375
    g12: LineSegment [constr] StartX=-29.5 StartY=12 StartZ=0 EndX=29.5 EndY=12 EndZ=0
    g13: LineSegment [constr] StartX=29.5 StartY=12 StartZ=0 EndX=29.5 EndY=-12 EndZ=0
    g14: LineSegment [constr] StartX=29.5 StartY=-12 StartZ=0 EndX=-29.5 EndY=-12 EndZ=0
    g15: LineSegment [constr] StartX=-29.5 StartY=-12 StartZ=0 EndX=-29.5 EndY=12 EndZ=0
    g16: ArcOfCircle [constr] CenterX=-29.5 CenterY=12 CenterZ=0 NormalX=0 NormalY=0 NormalZ=1 AngleXU=0 Radius=3 StartAngle=1.5708 EndAngle=3.14159
    g17: ArcOfCircle [constr] CenterX=29.5 CenterY=12 CenterZ=0 NormalX=0 NormalY=0 NormalZ=1 AngleXU=0 Radius=3 StartAngle=5.0002e-08 EndAngle=1.5708
    g18: ArcOfCircle [constr] CenterX=29.5 CenterY=-12 CenterZ=0 NormalX=0 NormalY=0 NormalZ=1 AngleXU=0 Radius=3 StartAngle=4.71239 EndAngle=6.28319
    g19: ArcOfCircle [constr] CenterX=-29.5 CenterY=-12 CenterZ=0 NormalX=0 NormalY=0 NormalZ=1 AngleXU=0 Radius=3 StartAngle=3.14159 EndAngle=4.71239
    g20: LineSegment [constr] StartX=-29.5 StartY=15 StartZ=0 EndX=29.5 EndY=15 EndZ=0
    g21: LineSegment [constr] StartX=32.5 StartY=12 StartZ=0 EndX=32.5 EndY=-12 EndZ=0
    g22: LineSegment [constr] StartX=29.5 StartY=-15 StartZ=0 EndX=-29.5 EndY=-15 EndZ=0
    g23: LineSegment [constr] StartX=-32.5 StartY=-12 StartZ=0 EndX=-32.5 EndY=12 EndZ=0
    g24: LineSegment [constr] StartX=25.3417 StartY=8.13712 StartZ=0 EndX=27.8417 EndY=8.13712 EndZ=0
    g25: LineSegment [constr] StartX=27.8417 StartY=8.13712 StartZ=0 EndX=27.8417 EndY=-1.46288 EndZ=0
    g26: LineSegment [constr] StartX=27.8417 StartY=-1.46288 StartZ=0 EndX=25.3417 EndY=-1.46288 EndZ=0
    g27: LineSegment [constr] StartX=25.3417 StartY=-1.46288 StartZ=0 EndX=25.3417 EndY=8.13712 EndZ=0
    g28: LineSegment [constr] StartX=25.3417 StartY=6.93712 StartZ=0 EndX=27.8417 EndY=6.93712 EndZ=0
    g29: LineSegment [constr] StartX=25.3417 StartY=5.73712 StartZ=0 EndX=27.8417 EndY=5.73712 EndZ=0
    g30: LineSegment [constr] StartX=25.3417 StartY=4.53712 StartZ=0 EndX=27.8417 EndY=4.53712 EndZ=0
    g31: LineSegment [constr] StartX=25.3417 StartY=3.33712 StartZ=0 EndX=27.8417 EndY=3.33712 EndZ=0
    g32: LineSegment [constr] StartX=25.3417 StartY=2.13712 StartZ=0 EndX=27.8417 EndY=2.13712 EndZ=0
    g33: LineSegment [constr] StartX=25.3417 StartY=0.937121 StartZ=0 EndX=27.8417 EndY=0.937121 EndZ=0
    g34: LineSegment [constr] StartX=25.3417 StartY=-0.262879 StartZ=0 EndX=27.8417 EndY=-0.262879 EndZ=0
    g35: ArcOfCircle CenterX=25.3417 CenterY=8.13712 CenterZ=0 NormalX=0 NormalY=0 NormalZ=1 AngleXU=0 Radius=0.75 StartAngle=1.12328 EndAngle=4.26487
    g36: ArcOfCircle CenterX=27.8417 CenterY=6.93712 CenterZ=0 NormalX=0 NormalY=0 NormalZ=1 AngleXU=0 Radius=0.75 StartAngle=4.26487 EndAngle=7.40646
    g37: Circle [constr] CenterX=27.8417 CenterY=6.93712 CenterZ=0 NormalX=0 NormalY=0 NormalZ=1 AngleXU=0 Radius=0.75
    g38: Circle [constr] CenterX=25.3417 CenterY=8.13712 CenterZ=0 NormalX=0 NormalY=0 NormalZ=1 AngleXU=0 Radius=0.75
    g39: LineSegment [constr] StartX=25.4338 StartY=8.92483 StartZ=0 EndX=28.7439 EndY=7.33601 EndZ=0
    g40: LineSegment [constr] StartX=24.2457 StartY=7.83129 StartZ=0 EndX=27.5618 EndY=6.23954 EndZ=0
    g41: LineSegment StartX=25.6663 StartY=8.81326 StartZ=0 EndX=28.1663 EndY=7.61326 EndZ=0
    g42: LineSegment StartX=25.0172 StartY=7.46098 StartZ=0 EndX=27.5172 EndY=6.26098 EndZ=0
    g43: ArcOfCircle CenterX=25.3417 CenterY=5.73712 CenterZ=0 NormalX=0 NormalY=0 NormalZ=1 AngleXU=0 Radius=0.75 StartAngle=1.12852 EndAngle=4.25962
    g44: LineSegment StartX=25.6627 StartY=6.41496 StartZ=0 EndX=28.149 EndY=5.22128 EndZ=0
    g45: ArcOfCircle CenterX=27.8417 CenterY=4.53712 CenterZ=0 NormalX=0 NormalY=0 NormalZ=1 AngleXU=0 Radius=0.75 StartAngle=4.23957 EndAngle=7.43184
    g46: LineSegment StartX=25.0136 StartY=5.06269 StartZ=0 EndX=27.5002 EndY=3.86941 EndZ=0
    g47: Circle CenterX=25.3417 CenterY=-1.46288 CenterZ=0 NormalX=0 NormalY=0 NormalZ=1 AngleXU=0 Radius=0.75
    g48: Circle CenterX=27.8417 CenterY=-0.262879 CenterZ=0 NormalX=0 NormalY=0 NormalZ=1 AngleXU=0 Radius=0.75
    g49: Circle CenterX=25.3417 CenterY=0.937121 CenterZ=0 NormalX=0 NormalY=0 NormalZ=1 AngleXU=0 Radius=0.75
    g50: Circle CenterX=27.8417 CenterY=2.13712 CenterZ=0 NormalX=0 NormalY=0 NormalZ=1 AngleXU=0 Radius=0.75
    g51: Circle CenterX=25.3417 CenterY=3.33712 CenterZ=0 NormalX=0 NormalY=0 NormalZ=1 AngleXU=0 Radius=0.75
    g52: LineSegment [constr] StartX=25.8911 StartY=-2.0311 StartZ=0 EndX=28.1814 EndY=-0.931754 EndZ=0
    g53: LineSegment [constr] StartX=24.1632 StartY=-1.19664 StartZ=0 EndX=27.4908 EndY=0.400624 EndZ=0
    g54: LineSegment [constr] StartX=24.363 StartY=0.574977 StartZ=0 EndX=28.2413 EndY=-1.28662 EndZ=0
    g55: LineSegment [constr] StartX=25.6678 StartY=1.61253 StartZ=0 EndX=28.5751 EndY=0.217016 EndZ=0
    g56: LineSegment [constr] StartX=24.9997 StartY=-0.0589725 StartZ=0 EndX=28.6995 EndY=1.71693 EndZ=0
    g57: LineSegment [constr] StartX=24.1511 StartY=1.19754 StartZ=0 EndX=27.2971 EndY=2.70762 EndZ=0
    g58: LineSegment [constr] StartX=24.3738 StartY=2.96979 StartZ=0 EndX=27.5399 EndY=1.45005 EndZ=0
    g59: Circle [constr] CenterX=25.3417 CenterY=2.13712 CenterZ=0 NormalX=0 NormalY=0 NormalZ=1 AngleXU=0 Radius=0.331828
    g60: Circle [constr] CenterX=27.8417 CenterY=0.937121 CenterZ=0 NormalX=0 NormalY=0 NormalZ=1 AngleXU=0 Radius=0.331828
    g61: Circle [constr] CenterX=25.3417 CenterY=-0.262879 CenterZ=0 NormalX=0 NormalY=0 NormalZ=1 AngleXU=0 Radius=0.331828
  constraints (161):
    c: Coincident(g0,g1)
    c: Coincident(g1,g2)
    c: Coincident(g2,g3)
    c: Coincident(g3,g0)
    c: Horizontal(g2)
    c: Vertical(g3)
    c: DistanceX(g0,g0) = 65
    c: DistanceY(g1,g1) = 30
    c: Symmetric(g0,g0,g-2)
    c: Symmetric(g0,g1,g-1)
    c: Coincident(g4,g5)
    c: Coincident(g5,g6)
    c: Coincident(g6,g7)
    c: Coincident(g7,g4)
    c: Horizontal(g6)
    c: Vertical(g7)
    c: DistanceX(g4,g4) = 58
    c: DistanceY(g5,g5) = 23
    c: Symmetric(g4,g5,g-1)
    c: Symmetric(g4,g4,g-2)
    c: Coincident(g8,g4)
    c: Coincident(g9,g4)
    c: Coincident(g10,g5)
    c: Coincident(g11,g6)
    c: Radius(g11) = 1.375
    c: Radius(g8) = 1.375
    c: Radius(g9) = 1.375
    c: Radius(g10) = 1.375
    c: Coincident(g12,g13)
    c: Coincident(g13,g14)
    c: Coincident(g14,g15)
    c: Coincident(g15,g12)
    c: Horizontal(g12)
    c: Horizontal(g14)
    c: Vertical(g13)
    c: Vertical(g15)
    c: DistanceX(g4,g12) = 0.5
    c: DistanceY(g4,g12) = 0.5
    c: DistanceY(g13,g5) = 0.5
    c: DistanceX(g14,g6) = 0.5
    c: Coincident(g16,g12)
    c: Radius(g16) = 3
    c: Coincident(g17,g12)
    c: Radius(g17) = 3
    c: Coincident(g18,g13)
    c: Radius(g18) = 3
    c: Coincident(g19,g14)
    c: Radius(g19) = 3
    c: PointOnObject(g16,g0)
    c: PointOnObject(g17,g1)
    c: PointOnObject(g18,g2)
    c: PointOnObject(g19,g3)
    c: Coincident(g20,g16)
    c: Horizontal(g20)
    c: Coincident(g20,g17)
    c: Coincident(g21,g17)
    c: Vertical(g21)
    c: Coincident(g18,g21)
    c: Coincident(g22,g18)
    c: Horizontal(g22)
    c: Coincident(g19,g22)
    c: Coincident(g23,g19)
    c: Vertical(g23)
    c: Coincident(g23,g16)
    c: Coincident(g24,g25)
    c: Coincident(g25,g26)
    c: Coincident(g26,g27)
    c: Coincident(g27,g24)
    c: Horizontal(g24)
    c: Horizontal(g26)
    c: Vertical(g25)
    c: Vertical(g27)
    c: DistanceX(g4,g24) = 54.3417  '3,362879'
    c: DistanceX(g24,g24) = 2.5
    c: DistanceY(g27,g27) = 9.6
    c: DistanceY(g24,g4) = 3.36288
    c: Horizontal(g28)
    c: Horizontal(g29)
    c: Horizontal(g30)
    c: Horizontal(g32)
    c: Horizontal(g33)
    c: DistanceY(g28,g24) = 1.2
    c: DistanceY(g29,g28) = 1.2
    c: DistanceY(g30,g29) = 1.2
    c: DistanceY(g31,g30) = 1.2
    c: DistanceY(g32,g31) = 1.2
    c: DistanceY(g33,g32) = 1.2
    c: Horizontal(g34)
    c: DistanceY(g34,g33) = 1.2
    c: PointOnObject(g28,g27)
    c: PointOnObject(g29,g27)
    c: PointOnObject(g30,g27)
    c: PointOnObject(g31,g27)
    c: PointOnObject(g32,g27)
    c: PointOnObject(g33,g27)
    c: PointOnObject(g34,g27)
    c: PointOnObject(g34,g25)
    c: PointOnObject(g33,g25)
    c: PointOnObject(g32,g25)
    c: PointOnObject(g31,g25)
    c: PointOnObject(g30,g25)
    c: PointOnObject(g29,g25)
    c: PointOnObject(g28,g25)
    c: Coincident(g35,g24)
    c: Coincident(g36,g28)
    c: Radius(g35) = 0.75
    c: Radius(g36) = 0.75
    c: Coincident(g37,g28)
    c: Coincident(g38,g24)
    c: Radius(g38) = 0.75
    c: Radius(g37) = 0.75
    c: Tangent(g39,g37)
    c: Tangent(g39,g38)
    c: Tangent(g40,g38)
    c: Tangent(g40,g37)
    c: PointOnObject(g41,g39)
    c: PointOnObject(g41,g39)
    c: PointOnObject(g42,g40)
    c: PointOnObject(g42,g40)
    c: Coincident(g41,g35)
    c: Coincident(g35,g42)
    c: Coincident(g41,g36)
    c: Coincident(g36,g42)
    c: Equal(g35,g43) = 0.75
    c: Equal(g36,g45) = 0.75
    c: Coincident(g44,g43)
    c: Coincident(g43,g46)
    c: Coincident(g44,g45)
    c: Coincident(g45,g46)
    c: Coincident(g43,g29)
    c: Coincident(g45,g30)
    c: Coincident(g48,g34)
    c: Coincident(g49,g33)
    c: Coincident(g50,g32)
    c: Coincident(g51,g31)
    c: Radius(g51) = 0.75
    c: Radius(g50) = 0.75
    c: Radius(g49) = 0.75
    c: Radius(g48) = 0.75
    c: Radius(g47) = 0.75
    c: Tangent(g55,g48)
    c: Tangent(g55,g49)
    c: Tangent(g54,g49)
    c: Tangent(g54,g48)
    c: Tangent(g53,g47)
    c: Tangent(g53,g48)
    c: Coincident(g47,g26)
    c: Tangent(g47,g52)
    c: Tangent(g52,g48)
    c: Tangent(g56,g49)
    c: Tangent(g56,g50)
    c: Tangent(g57,g50)
    c: Tangent(g57,g49)
    c: Tangent(g58,g51)
    c: Tangent(g58,g50)
    c: Coincident(g59,g32)
    c: Tangent(g59,g58)
    c: Coincident(g60,g33)
    c: Tangent(g60,g56)
    c: Coincident(g61,g34)
    c: Tangent(g61,g54)
FEATURE [PartDesign::Pocket] Pocket005
  BaseFeature = -> Pocket004
  Length = 5
  Length2 = 100
  Profile = -> Sketch009
  Type = 2
FEATURE [Part::Feature] path76
  shape: bbox 67.53 x 33.36 x 2e-07 mm, 1 faces, 0 solids (baked)
FEATURE [Part::Feature] path76001
  shape: bbox 56.51 x 33.36 x 2e-07 mm, 1 faces, 0 solids (baked)
FEATURE [Part::Feature] path76002
  shape: bbox 67.23 x 33.39 x 2e-07 mm, 1 faces, 0 solids (baked)
FEATURE [Part::Feature] path76003
  shape: bbox 86.8 x 33.05 x 2e-07 mm, 1 faces, 0 solids (baked)
FEATURE [Part::Feature] path76004
  shape: bbox 24.36 x 17.06 x 2e-07 mm, 1 faces, 0 solids (baked)
FEATURE [Part::Cut] Cut
  Base = -> path76003
  Tool = -> path76004
FEATURE [Part::MultiFuse] Fusion
  Shapes = -> [path76,path76001,path76002,Cut]
FEATURE [Part::FeaturePython] Scale001  # Draft clone (typed FeaturePython)
  Fuse = false
  Objects = -> [Fusion]
  Placement = pos=(-20,0,14.85) rot=(0,0,1;0rad)
  Scale = (0.18,0.18,0.18)
FEATURE [Sketcher::SketchObject] Sketch010
  MapMode = 5
  Placement = pos=(0,0,8.5) rot=(0,0,1;0rad)
FEATURE [Part::FeaturePython] Scale  # Draft clone (typed FeaturePython)
  Fuse = false
  Objects = -> [Scale001]
  Placement = pos=(-11.9,-2.3,7.95) rot=(0,0,1;0rad)
  Scale = (0.8,0.8,0.8)
FEATURE [PartDesign::Fillet] Fillet001
  Base = -> Pocket005 [Edge29,Edge25,Edge20,Edge34,Edge22,Edge21,Edge33,Edge107,Edge99,Edge88,Edge116,Edge92,Edge90,Edge114]
  BaseFeature = -> Pocket005
  Radius = 0.2
FEATURE [PartDesign::Fillet] Fillet003
  Base = -> Fillet001 [Edge24,Edge25,Edge30,Edge31]
  BaseFeature = -> Fillet001
  Radius = 0.1
FEATURE [PartDesign::Fillet] Fillet004
  Base = -> Fillet003 [Edge251,Edge253,Edge252,Edge247,Edge239]
  BaseFeature = -> Fillet003
  Radius = 0.1
FEATURE [PartDesign::Body] Body
  Group = -> [Sketch,Sketch001,Pad,Sketch002,Pocket,Sketch003,Pocket001,Sketch004,Sketch005,Pocket002,Sketch006,Pocket003,Fillet,Chamfer,Sketch007,Hole,Sketch008,Pocket004,Sketch009,Pocket005,Sketch010,Fillet001,Fillet003,Fillet004]
  Origin = -> Origin
  Tip = -> Fillet004
FEATURE [Part::Extrusion] Extrude
  Base = -> Scale
  Dir = (0,0,1)
  DirMode = 0
  FaceMakerClass = Part::FaceMakerBullseye
  LengthFwd = 5
  LengthRev = 0
  Solid = false
  Symmetric = false
FEATURE [Part::Cut] Cut001
  Base = -> Fillet004
  Tool = -> Extrude
FEATURE [Mesh::Feature] Mesh  label="Cut001 (Meshed)"
